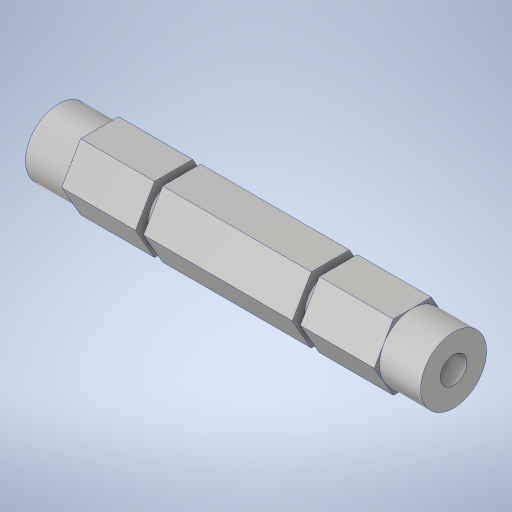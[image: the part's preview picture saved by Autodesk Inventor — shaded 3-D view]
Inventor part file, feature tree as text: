
AUTODESK INVENTOR PART (.ipt)
format: ipt  version: 2023.4 (Build 274418000, 418)  size: 297,984 bytes
history: native  units: in
note: dims shown in document units (in); Inventor stores cm internally (conversion verified against a paired STEP export)
features: sketch x5, extrude x3, projected_geometry x2, hole x1, revolve x1, mirror x1
ambient origin geometry x8: Origin, YZ Plane, XZ Plane, XY Plane, X Axis, Y Axis, Z Axis, Center Point
bodies: Solid1 (feature_tree)
feature tree (13):
  extrude  "Extrusion1"  Depth=2.374in TaperAngle=0.0deg
  extrude  "Extrusion2"  Depth=0.313in TaperAngle=0.0deg
  extrude  "Extrusion3"  Depth=0.313in TaperAngle=0.0deg
  hole  "Hole1"  [1 undecoded]
  revolve  "Revolution1"  [1 undecoded]
  mirror  "Mirror1"
  sketch  "Sketch1"  dims[d0=0.5in d1=2.374in d2=0.0in]
  sketch  "Sketch2"  dims[d3=0.5in d4=0.313in d5=0.0in]
  sketch  "Sketch3"  dims[d6=0.5in d7=0.313in d8=0.0in]
  sketch  "Sketch4"  dims[d9=0.201in d10=0.75in d11=0.385in d12=0.25in d13=0.5635in d14=1.0in d15=0.8108in d16=0.392in]
  projected_geometry  "Projected Loop1"
  sketch  "Sketch6"  dims[d17=0.06in d18=0.875in d19=90.0deg]
  projected_geometry  "Project Cut Edges1"
note: 2 required parameter values undecoded (feature->parameter linkage not recoverable at this tier; creation-order binding heuristic only, values carry confidence <= 0.55)